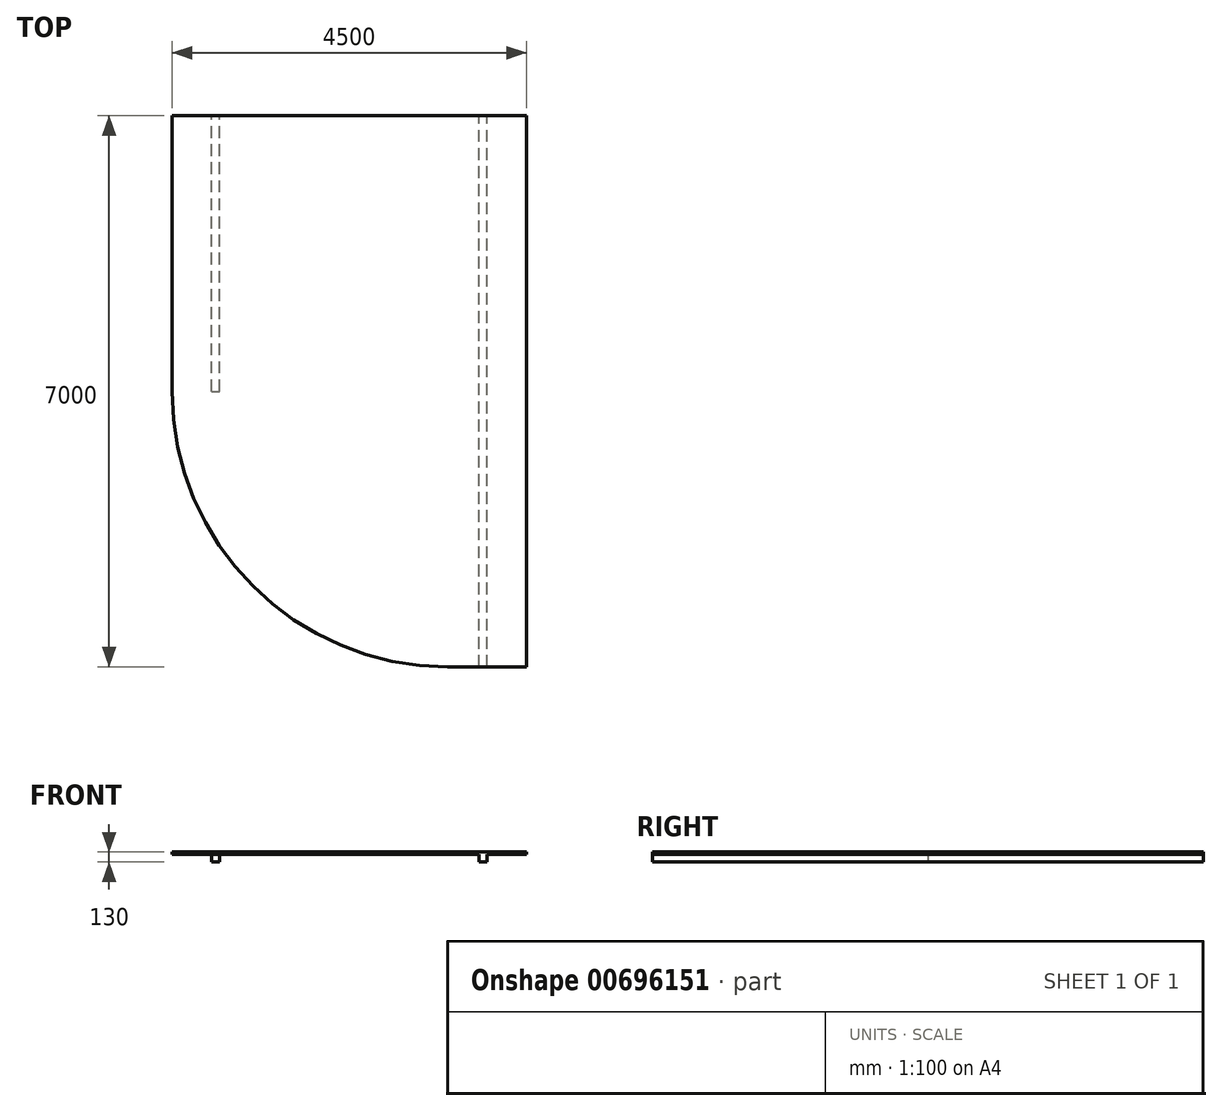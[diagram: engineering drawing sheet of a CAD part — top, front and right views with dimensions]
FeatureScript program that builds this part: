
annotation { "Feature Type Name" : "Feature", "Feature Type Description" : "" }
export const myFeature = defineFeature(function(context is Context, id is Id, definition is map)
    precondition{}
    {
        {
            var Q0;
            Q0=qCreatedBy(makeId("Top.planeOp"),FACE);
            var sketch = newSketch(context, id + "F0", { "sketchPlane" : qUnion([Q0])});
            skLineSegment(sketch, "E0.bottom", {"start": v(1522.58, -4157.27) * mm, "end": v(2522.58, -4157.27) * mm});
            skLineSegment(sketch, "E0.top", {"start": v(-1977.42, 2842.73) * mm, "end": v(2522.58, 2842.73) * mm});
            skLineSegment(sketch, "E0.left", {"start": v(-1977.42, -657.27) * mm, "end": v(-1977.42, 2842.73) * mm});
            skLineSegment(sketch, "E0.right", {"start": v(2522.58, -4157.27) * mm, "end": v(2522.58, 2842.73) * mm});
            skPoint(sketch, "E1.visualSharp", {"position": v(-1977.42, -4157.27) * mm});
            skArc(sketch, "E1.filletArc", {"start": v(-1977.42, -657.27) * mm, "mid": v(-952.29, -3132.14) * mm, "end": v(1522.58, -4157.27) * mm});
            skSolve(sketch);
        }
        {
            var Q0;
            Q0 = qSketchRegion(id + "F0", true);
            extrude(context, id + "F1", {"entities" : qUnion([Q0]), "oppositeDirection" : true, "depth" : 30 * mm, "offsetDistance" : 25 * mm});
        }
        {
            var Q0;
            Q0=makeQuery(id+"F1.opExtrude","SWEPT_FACE",FACE,{"disambiguationData":[OSD([sQuery(id+"F0.wireOp",EDGE,"E0.top")])]});
            var sketch = newSketch(context, id + "F2", { "sketchPlane" : qUnion([Q0])});
            skLineSegment(sketch, "E2.bottom", {"start": v(-2022.58, -30) * mm, "end": v(-1922.58, -30) * mm});
            skLineSegment(sketch, "E2.top", {"start": v(-2022.58, -130) * mm, "end": v(-1922.58, -130) * mm});
            skLineSegment(sketch, "E2.left", {"start": v(-2022.58, -30) * mm, "end": v(-2022.58, -130) * mm});
            skLineSegment(sketch, "E2.right", {"start": v(-1922.58, -30) * mm, "end": v(-1922.58, -130) * mm});
            skSolve(sketch);
        }
        {
            var Q0;
            Q0 = qSketchRegion(id + "F2", true);
            var Q1;
            Q1=makeQuery(id+"F1.opExtrude","SWEPT_FACE",FACE,{"disambiguationData":[OSD([sQuery(id+"F0.wireOp",EDGE,"E0.bottom")])]});
            extrude(context, id + "F3", {"entities" : qUnion([Q0]), "operationType" : NewBodyOperationType.ADD, "endBound" : BoundingType.UP_TO_SURFACE, "oppositeDirection" : true, "depth" : 25 * mm, "endBoundEntityFace" : qUnion([Q1]), "offsetDistance" : 25 * mm});
        }
        {
            var Q0;
            Q0=makeQuery(id+"F3.boolean.opBoolean","MERGE",FACE,{"derivedFrom":[makeQuery(id+"F1.opExtrude","SWEPT_FACE",FACE,{"disambiguationData":[OSD([sQuery(id+"F0.wireOp",EDGE,"E0.top")])]}),makeQuery(id+"F3.opExtrude","CAP_FACE",FACE,{"disambiguationData":[OSD([sQuery(id+"F2.wireOp",EDGE,"E2.bottom"),sQuery(id+"F2.wireOp",EDGE,"E2.top"),sQuery(id+"F2.wireOp",EDGE,"E2.left"),sQuery(id+"F2.wireOp",EDGE,"E2.right")])],"isStart":true})]});
            var sketch = newSketch(context, id + "F4", { "sketchPlane" : qUnion([Q0])});
            skLineSegment(sketch, "E3.bottom", {"start": v(1477.42, -30) * mm, "end": v(1377.42, -30) * mm});
            skLineSegment(sketch, "E3.top", {"start": v(1477.42, -130) * mm, "end": v(1377.42, -130) * mm});
            skLineSegment(sketch, "E3.left", {"start": v(1477.42, -30) * mm, "end": v(1477.42, -130) * mm});
            skLineSegment(sketch, "E3.right", {"start": v(1377.42, -30) * mm, "end": v(1377.42, -130) * mm});
            skSolve(sketch);
        }
        {
            var Q0;
            Q0 = qSketchRegion(id + "F4", true);
            extrude(context, id + "F5", {"entities" : qUnion([Q0]), "operationType" : NewBodyOperationType.ADD, "oppositeDirection" : true, "depth" : 3500 * mm, "offsetDistance" : 25 * mm});
        }
    });
